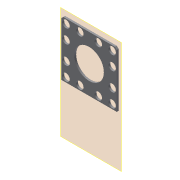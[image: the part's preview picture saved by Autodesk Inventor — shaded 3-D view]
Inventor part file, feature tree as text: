
AUTODESK INVENTOR PART (.ipt)
format: ipt  version: 2019.4 (Build 234330000, 330)  size: 122,368 bytes
history: native  units: mm
features: reference x2, other x2, plane x1, extrude x1, sketch x1
ambient origin geometry x8: Origin, YZ Plane, XZ Plane, XY Plane, X Axis, Y Axis, Z Axis, Center Point
bodies: Solid1 (feature_tree)
feature tree (7):
  plane  "Work Plane1"
  extrude  "Extrusion1"  [1 undecoded]
  sketch  "Sketch1"  dims[d0=2.0mm d1=0.0mm]
  reference  "Reference1"
  reference  "Reference2"
  other  "Assembly_XY_stage_with_motors_v3.iam"
  other  "30_XY_Sample_arm_v3:1"
note: 1 required parameter value undecoded (feature->parameter linkage not recoverable at this tier; creation-order binding heuristic only, values carry confidence <= 0.55)
